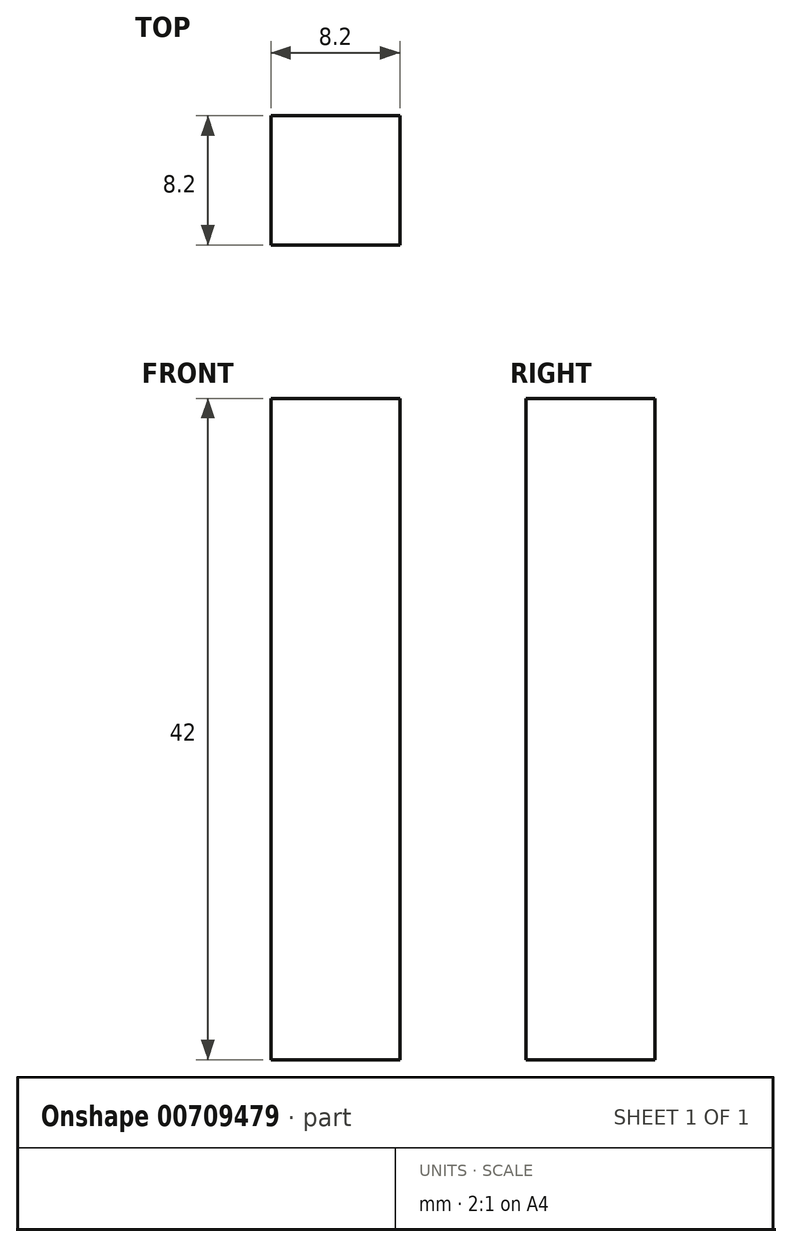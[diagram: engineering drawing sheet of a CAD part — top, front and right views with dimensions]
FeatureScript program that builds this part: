
annotation { "Feature Type Name" : "Feature", "Feature Type Description" : "" }
export const myFeature = defineFeature(function(context is Context, id is Id, definition is map)
    precondition{}
    {
        {
            var Q0;
            Q0=qCreatedBy(makeId("Top.planeOp"),FACE);
            var sketch = newSketch(context, id + "F0", { "sketchPlane" : qUnion([Q0])});
            skLineSegment(sketch, "E0.bottom", {"start": v(4.1, 4.1) * mm, "end": v(-4.1, 4.1) * mm});
            skLineSegment(sketch, "E0.top", {"start": v(4.1, -4.1) * mm, "end": v(-4.1, -4.1) * mm});
            skLineSegment(sketch, "E0.left", {"start": v(4.1, 4.1) * mm, "end": v(4.1, -4.1) * mm});
            skLineSegment(sketch, "E0.right", {"start": v(-4.1, 4.1) * mm, "end": v(-4.1, -4.1) * mm});
            skPoint(sketch, "E0.middle", {"position": v(0, 0) * mm});
            skSolve(sketch);
        }
        {
            var Q0;
            Q0 = qSketchRegion(id + "F0", true);
            extrude(context, id + "F1", {"entities" : qUnion([Q0]), "depth" : 42 * mm, "offsetDistance" : 25.4 * mm});
        }
    });
